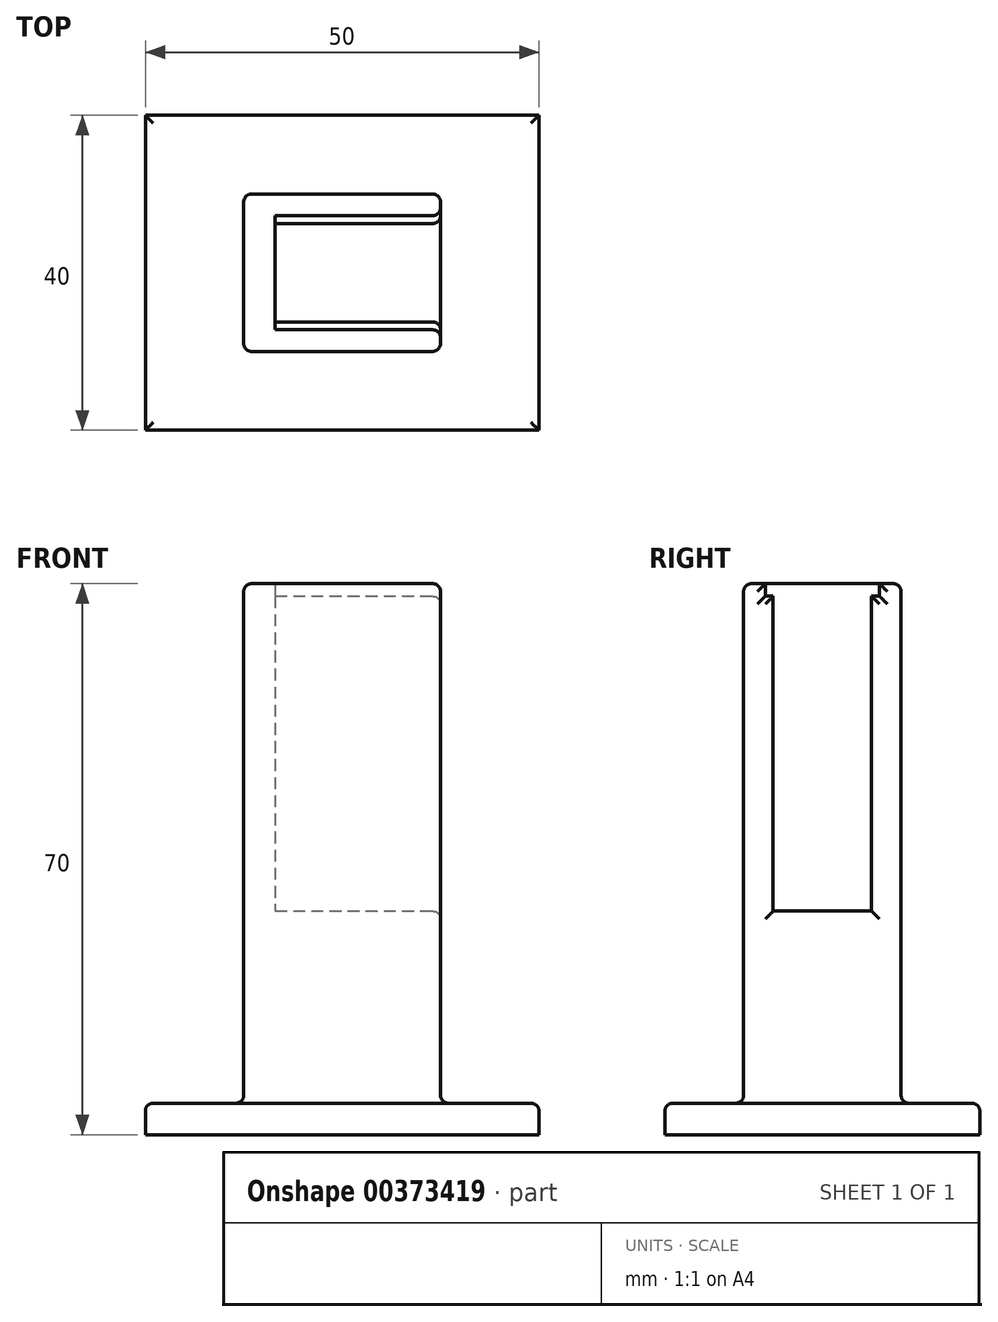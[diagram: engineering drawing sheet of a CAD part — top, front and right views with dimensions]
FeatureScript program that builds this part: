
annotation { "Feature Type Name" : "Feature", "Feature Type Description" : "" }
export const myFeature = defineFeature(function(context is Context, id is Id, definition is map)
    precondition{}
    {
        {
            var Q0;
            Q0=qCreatedBy(makeId("Top.planeOp"),FACE);
            var sketch = newSketch(context, id + "F0", { "sketchPlane" : qUnion([Q0])});
            skLineSegment(sketch, "E0.bottom", {"start": v(12.5, -10) * mm, "end": v(-12.5, -10) * mm});
            skLineSegment(sketch, "E0.top", {"start": v(12.5, 10) * mm, "end": v(-12.5, 10) * mm});
            skLineSegment(sketch, "E0.left", {"start": v(12.5, -10) * mm, "end": v(12.5, 10) * mm});
            skLineSegment(sketch, "E0.right", {"start": v(-12.5, -10) * mm, "end": v(-12.5, 10) * mm});
            skPoint(sketch, "E0.middle", {"position": v(0, 0) * mm});
            skSolve(sketch);
        }
        {
            var Q0;
            Q0 = qSketchRegion(id + "F0", true);
            extrude(context, id + "F1", {"entities" : qUnion([Q0]), "depth" : 70 * mm});
        }
        {
            var Q0;
            Q0=makeQuery(id+"F1.opExtrude","SWEPT_FACE",FACE,{"disambiguationData":[OSD([sQuery(id+"F0.wireOp",EDGE,"E0.left")])]});
            var sketch = newSketch(context, id + "F2", { "sketchPlane" : qUnion([Q0])});
            skLineSegment(sketch, "E1.bottom", {"start": v(-7.25, 70) * mm, "end": v(7.25, 70) * mm});
            skLineSegment(sketch, "E1.top", {"start": v(-7.25, 68.4) * mm, "end": v(-6.25, 68.4) * mm});
            skLineSegment(sketch, "E1.left", {"start": v(-7.25, 70) * mm, "end": v(-7.25, 68.4) * mm});
            skLineSegment(sketch, "E1.right", {"start": v(7.25, 70) * mm, "end": v(7.25, 68.4) * mm});
            skLineSegment(sketch, "E2.top", {"start": v(-6.25, 28.4) * mm, "end": v(6.25, 28.4) * mm});
            skLineSegment(sketch, "E2.left", {"start": v(-6.25, 68.4) * mm, "end": v(-6.25, 28.4) * mm});
            skLineSegment(sketch, "E2.right", {"start": v(6.25, 68.4) * mm, "end": v(6.25, 28.4) * mm});
            skLineSegment(sketch, "E3.trimOffspring", {"start": v(6.25, 68.4) * mm, "end": v(7.25, 68.4) * mm});
            skSolve(sketch);
        }
        {
            var Q0;
            Q0 = qSketchRegion(id + "F2", true);
            extrude(context, id + "F3", {"entities" : qUnion([Q0]), "operationType" : NewBodyOperationType.REMOVE, "oppositeDirection" : true, "depth" : 21 * mm});
        }
        {
            var Q0;
            Q0=makeQuery(id+"F1.opExtrude","CAP_FACE",FACE,{"disambiguationData":[OSD([sQuery(id+"F0.wireOp",EDGE,"E0.bottom"),sQuery(id+"F0.wireOp",EDGE,"E0.top"),sQuery(id+"F0.wireOp",EDGE,"E0.left"),sQuery(id+"F0.wireOp",EDGE,"E0.right")])],"isStart":true});
            var sketch = newSketch(context, id + "F4", { "sketchPlane" : qUnion([Q0])});
            skLineSegment(sketch, "E4.bottom", {"start": v(25, -20) * mm, "end": v(-25, -20) * mm});
            skLineSegment(sketch, "E4.top", {"start": v(25, 20) * mm, "end": v(-25, 20) * mm});
            skLineSegment(sketch, "E4.left", {"start": v(25, -20) * mm, "end": v(25, 20) * mm});
            skLineSegment(sketch, "E4.right", {"start": v(-25, -20) * mm, "end": v(-25, 20) * mm});
            skPoint(sketch, "E4.middle", {"position": v(0, 0) * mm});
            skSolve(sketch);
        }
        {
            var Q0;
            Q0 = qSketchRegion(id + "F4", true);
            extrude(context, id + "F5", {"entities" : qUnion([Q0]), "operationType" : NewBodyOperationType.ADD, "oppositeDirection" : true, "depth" : 4 * mm});
        }
        {
            var Q0;
            Q0=makeQuery(id+"F5.opExtrude","CAP_FACE",FACE,{"disambiguationData":[OSD([sQuery(id+"F4.wireOp",EDGE,"E4.bottom"),sQuery(id+"F4.wireOp",EDGE,"E4.top"),sQuery(id+"F4.wireOp",EDGE,"E4.left"),sQuery(id+"F4.wireOp",EDGE,"E4.right")])],"isStart":false});
            var Q1;
            Q1=makeQuery(id+"F1.opExtrude","SWEPT_FACE",FACE,{"disambiguationData":[OSD([sQuery(id+"F0.wireOp",EDGE,"E0.left")])]});
            var Q2;
            Q2=makeQuery(id+"F1.opExtrude","SWEPT_FACE",FACE,{"disambiguationData":[OSD([sQuery(id+"F0.wireOp",EDGE,"E0.top")])]});
            var Q3;
            Q3=makeQuery(id+"F1.opExtrude","SWEPT_FACE",FACE,{"disambiguationData":[OSD([sQuery(id+"F0.wireOp",EDGE,"E0.right")])]});
            var Q4;
            Q4=makeQuery(id+"F1.opExtrude","SWEPT_FACE",FACE,{"disambiguationData":[OSD([sQuery(id+"F0.wireOp",EDGE,"E0.bottom")])]});
            fillet(context, id + "F6", {"entities" : qUnion([Q0, Q1, Q2, Q3, Q4]), "radius" : 1 * mm, "tangentPropagation" : true, "allowEdgeOverflow" : false});
        }
    });
